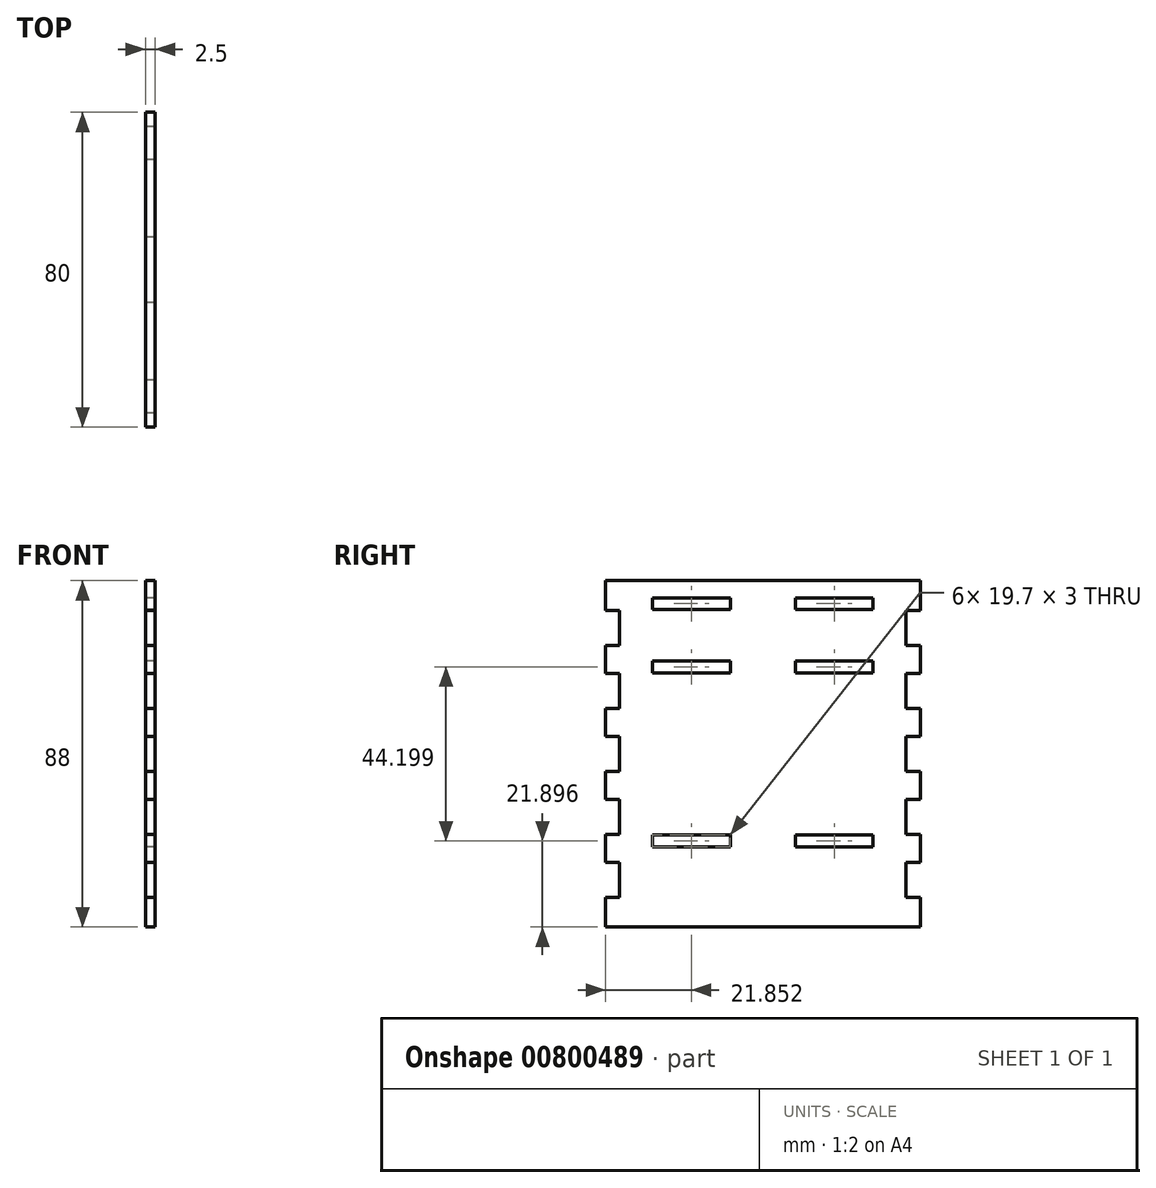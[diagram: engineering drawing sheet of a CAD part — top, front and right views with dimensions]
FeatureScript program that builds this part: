
annotation { "Feature Type Name" : "Feature", "Feature Type Description" : "" }
export const myFeature = defineFeature(function(context is Context, id is Id, definition is map)
    precondition{}
    {
        {
            var Q0;
            Q0=qCreatedBy(makeId("Right.planeOp"),FACE);
            var sketch = newSketch(context, id + "F0", { "sketchPlane" : qUnion([Q0])});
            skLineSegment(sketch, "E0.top", {"start": v(-36.4, -44) * mm, "end": v(36.4, -44) * mm});
            skLineSegment(sketch, "E0.left", {"start": v(-36.4, 44) * mm, "end": v(-36.4, -44) * mm});
            skLineSegment(sketch, "E0.right", {"start": v(36.4, 44) * mm, "end": v(36.4, -44) * mm});
            skPoint(sketch, "E0.middle", {"position": v(0, 0) * mm});
            skLineSegment(sketch, "E1", {"start": v(-36.4, 44) * mm, "end": v(-40, 44) * mm});
            skLineSegment(sketch, "E2", {"start": v(-40, 44) * mm, "end": v(-40, 36.4) * mm});
            skLineSegment(sketch, "E3", {"start": v(-40, 36.4) * mm, "end": v(-36.4, 36.4) * mm});
            skLineSegment(sketch, "E4", {"start": v(-36.4, 36.4) * mm, "end": v(-36.4, 27.6) * mm});
            skLineSegment(sketch, "E5", {"start": v(-36.4, 27.6) * mm, "end": v(-40, 27.6) * mm});
            skLineSegment(sketch, "E6", {"start": v(-40, 27.6) * mm, "end": v(-40, 20.4) * mm});
            skLineSegment(sketch, "E7", {"start": v(-40, 20.4) * mm, "end": v(-36.4, 20.4) * mm});
            skLineSegment(sketch, "E8", {"start": v(-36.4, 20.4) * mm, "end": v(-36.4, 11.6) * mm});
            skLineSegment(sketch, "E9", {"start": v(-36.4, 11.6) * mm, "end": v(-40, 11.6) * mm});
            skLineSegment(sketch, "E10", {"start": v(-40, 11.6) * mm, "end": v(-40, 4.4) * mm});
            skLineSegment(sketch, "E11", {"start": v(-40, 4.4) * mm, "end": v(-36.4, 4.4) * mm});
            skLineSegment(sketch, "E12.MirrorCS", {"start": v(-36.4, -44) * mm, "end": v(-40, -44) * mm});
            skLineSegment(sketch, "E13.MirrorCS", {"start": v(-40, -44) * mm, "end": v(-40, -36.4) * mm});
            skLineSegment(sketch, "E14.MirrorCS", {"start": v(-40, -36.4) * mm, "end": v(-36.4, -36.4) * mm});
            skLineSegment(sketch, "E15.MirrorCS", {"start": v(-36.4, -27.6) * mm, "end": v(-40, -27.6) * mm});
            skLineSegment(sketch, "E16.MirrorCS", {"start": v(-40, -20.4) * mm, "end": v(-36.4, -20.4) * mm});
            skLineSegment(sketch, "E17.MirrorCS", {"start": v(-40, -27.6) * mm, "end": v(-40, -20.4) * mm});
            skLineSegment(sketch, "E18", {"start": v(-36.4, 4.4) * mm, "end": v(-36.4, -4.4) * mm});
            skLineSegment(sketch, "E19", {"start": v(-36.4, -4.4) * mm, "end": v(-40, -4.4) * mm});
            skLineSegment(sketch, "E20", {"start": v(-40, -4.4) * mm, "end": v(-40, -11.6) * mm});
            skLineSegment(sketch, "E21", {"start": v(-40, -11.6) * mm, "end": v(-36.4, -11.6) * mm});
            skLineSegment(sketch, "E22.MirrorCS", {"start": v(36.4, 44) * mm, "end": v(40, 44) * mm});
            skLineSegment(sketch, "E23.MirrorCS", {"start": v(40, 44) * mm, "end": v(40, 36.4) * mm});
            skLineSegment(sketch, "E24.MirrorCS", {"start": v(40, 36.4) * mm, "end": v(36.4, 36.4) * mm});
            skLineSegment(sketch, "E25.MirrorCS", {"start": v(36.4, 27.6) * mm, "end": v(40, 27.6) * mm});
            skLineSegment(sketch, "E26.MirrorCS", {"start": v(40, 27.6) * mm, "end": v(40, 20.4) * mm});
            skLineSegment(sketch, "E27.MirrorCS", {"start": v(40, 20.4) * mm, "end": v(36.4, 20.4) * mm});
            skLineSegment(sketch, "E28.MirrorCS", {"start": v(36.4, 11.6) * mm, "end": v(40, 11.6) * mm});
            skLineSegment(sketch, "E29.MirrorCS", {"start": v(40, 11.6) * mm, "end": v(40, 4.4) * mm});
            skLineSegment(sketch, "E30.MirrorCS", {"start": v(40, 4.4) * mm, "end": v(36.4, 4.4) * mm});
            skLineSegment(sketch, "E31.MirrorCS", {"start": v(36.4, -4.4) * mm, "end": v(40, -4.4) * mm});
            skLineSegment(sketch, "E32.MirrorCS", {"start": v(40, -4.4) * mm, "end": v(40, -11.6) * mm});
            skLineSegment(sketch, "E33.MirrorCS", {"start": v(40, -11.6) * mm, "end": v(36.4, -11.6) * mm});
            skLineSegment(sketch, "E34.MirrorCS", {"start": v(40, -20.4) * mm, "end": v(36.4, -20.4) * mm});
            skLineSegment(sketch, "E35.MirrorCS", {"start": v(40, -27.6) * mm, "end": v(40, -20.4) * mm});
            skLineSegment(sketch, "E36.MirrorCS", {"start": v(36.4, -27.6) * mm, "end": v(40, -27.6) * mm});
            skLineSegment(sketch, "E37.MirrorCS", {"start": v(40, -36.4) * mm, "end": v(36.4, -36.4) * mm});
            skLineSegment(sketch, "E38.MirrorCS", {"start": v(40, -44) * mm, "end": v(40, -36.4) * mm});
            skLineSegment(sketch, "E39.MirrorCS", {"start": v(36.4, -44) * mm, "end": v(40, -44) * mm});
            skPoint(sketch, "E40.middle", {"position": v(-18.15, 38.16) * mm});
            skPoint(sketch, "E41.middle", {"position": v(-18.15, 22.1) * mm});
            skPoint(sketch, "E42.middle", {"position": v(-18.15, -22.1) * mm});
            skLineSegment(sketch, "E43", {"start": v(-36.4, 44) * mm, "end": v(36.4, 44) * mm});
            skLineSegment(sketch, "E44.bottom", {"start": v(-8.3, 36.66) * mm, "end": v(-28, 36.66) * mm});
            skLineSegment(sketch, "E44.top", {"start": v(-8.3, 39.66) * mm, "end": v(-28, 39.66) * mm});
            skLineSegment(sketch, "E44.left", {"start": v(-8.3, 36.66) * mm, "end": v(-8.3, 39.66) * mm});
            skLineSegment(sketch, "E44.right", {"start": v(-28, 36.66) * mm, "end": v(-28, 39.66) * mm});
            skLineSegment(sketch, "E45.bottom", {"start": v(-8.3, 20.6) * mm, "end": v(-28, 20.6) * mm});
            skLineSegment(sketch, "E45.top", {"start": v(-8.3, 23.6) * mm, "end": v(-28, 23.6) * mm});
            skLineSegment(sketch, "E45.left", {"start": v(-8.3, 20.6) * mm, "end": v(-8.3, 23.6) * mm});
            skLineSegment(sketch, "E45.right", {"start": v(-28, 20.6) * mm, "end": v(-28, 23.6) * mm});
            skLineSegment(sketch, "E46.bottom", {"start": v(-28, -20.6) * mm, "end": v(-8.3, -20.6) * mm});
            skLineSegment(sketch, "E46.top", {"start": v(-28, -23.6) * mm, "end": v(-8.3, -23.6) * mm});
            skLineSegment(sketch, "E46.left", {"start": v(-28, -20.6) * mm, "end": v(-28, -23.6) * mm});
            skLineSegment(sketch, "E46.right", {"start": v(-8.3, -20.6) * mm, "end": v(-8.3, -23.6) * mm});
            skLineSegment(sketch, "E47.MirrorCS", {"start": v(8.3, 20.6) * mm, "end": v(8.3, 23.6) * mm});
            skLineSegment(sketch, "E48.MirrorCS", {"start": v(8.3, -20.6) * mm, "end": v(8.3, -23.6) * mm});
            skLineSegment(sketch, "E49.MirrorCS", {"start": v(28, 36.66) * mm, "end": v(28, 39.66) * mm});
            skLineSegment(sketch, "E50.MirrorCS", {"start": v(28, -20.6) * mm, "end": v(28, -23.6) * mm});
            skLineSegment(sketch, "E51.MirrorCS", {"start": v(28, 20.6) * mm, "end": v(28, 23.6) * mm});
            skLineSegment(sketch, "E52.MirrorCS", {"start": v(8.3, 36.66) * mm, "end": v(8.3, 39.66) * mm});
            skPoint(sketch, "E53.MirrorP", {"position": v(18.15, 38.16) * mm});
            skPoint(sketch, "E54.MirrorP", {"position": v(18.15, 22.1) * mm});
            skPoint(sketch, "E55.MirrorP", {"position": v(18.15, -22.1) * mm});
            skLineSegment(sketch, "E56.MirrorCS", {"start": v(8.3, 20.6) * mm, "end": v(28, 20.6) * mm});
            skLineSegment(sketch, "E57.MirrorCS", {"start": v(28, -20.6) * mm, "end": v(8.3, -20.6) * mm});
            skLineSegment(sketch, "E58.MirrorCS", {"start": v(8.3, 39.66) * mm, "end": v(28, 39.66) * mm});
            skLineSegment(sketch, "E59.MirrorCS", {"start": v(28, -23.6) * mm, "end": v(8.3, -23.6) * mm});
            skLineSegment(sketch, "E60.MirrorCS", {"start": v(8.3, 36.66) * mm, "end": v(28, 36.66) * mm});
            skLineSegment(sketch, "E61.MirrorCS", {"start": v(8.3, 23.6) * mm, "end": v(28, 23.6) * mm});
            skSolve(sketch);
        }
        {
            var Q0;
            {var subQ7=sQuery(id+"F0.wireOp",EDGE,"nzJml5v2-Lp1t-HL96-k7b3-nT1KXYDu2QD1.bottom");Q0=makeQuery(id+"F0.imprint","IMPRINT",FACE,{"disambiguationData":[TD([[makeQuery(id+"F0.imprint","IMPRINT",EDGE,{"derivedFrom":subQ7}),-1.0]])]});}
            var Q1;
            {var subQ3=sQuery(id+"F0.wireOp",EDGE,"E9");var subQ9=sQuery(id+"F0.wireOp",EDGE,"E25.MirrorCS");var subQ12=sQuery(id+"F0.wireOp",EDGE,"E5");var subQ17=sQuery(id+"F0.wireOp",EDGE,"E28.MirrorCS");var subQ22=sQuery(id+"F0.wireOp",EDGE,"E15.MirrorCS");var subQ29=sQuery(id+"F0.wireOp",EDGE,"E34.MirrorCS");var subQ32=sQuery(id+"F0.wireOp",EDGE,"E19");var subQ38=sQuery(id+"F0.wireOp",EDGE,"E1");var subQ42=sQuery(id+"F0.wireOp",EDGE,"E12.MirrorCS");var subQ43=sQuery(id+"F0.wireOp",EDGE,"E0.top");var subQ47=sQuery(id+"F0.wireOp",EDGE,"E37.MirrorCS");var subQ51=sQuery(id+"F0.wireOp",EDGE,"E31.MirrorCS");var subQ57=sQuery(id+"F0.wireOp",EDGE,"E22.MirrorCS");Q1=qUnion([makeQuery(id+"F0.imprint","IMPRINT",FACE,{"disambiguationData":[TD([[makeQuery(id+"F0.imprint","IMPRINT",EDGE,{"derivedFrom":subQ47}),1.0]])]}),makeQuery(id+"F0.imprint","IMPRINT",FACE,{"disambiguationData":[TD([[makeQuery(id+"F0.imprint","IMPRINT",EDGE,{"derivedFrom":subQ42}),-1.0]])]}),makeQuery(id+"F0.imprint","IMPRINT",FACE,{"disambiguationData":[TD([[makeQuery(id+"F0.imprint","IMPRINT",EDGE,{"derivedFrom":subQ57}),-1.0]])]}),makeQuery(id+"F0.imprint","IMPRINT",FACE,{"disambiguationData":[TD([[makeQuery(id+"F0.imprint","IMPRINT",EDGE,{"derivedFrom":subQ38}),1.0]])]}),makeQuery(id+"F0.imprint","IMPRINT",FACE,{"disambiguationData":[TD([[makeQuery(id+"F0.imprint","IMPRINT",EDGE,{"derivedFrom":subQ51}),-1.0]])]}),makeQuery(id+"F0.imprint","IMPRINT",FACE,{"disambiguationData":[TD([[makeQuery(id+"F0.imprint","IMPRINT",EDGE,{"derivedFrom":subQ32}),1.0]])]}),makeQuery(id+"F0.imprint","IMPRINT",FACE,{"disambiguationData":[TD([[makeQuery(id+"F0.imprint","IMPRINT",EDGE,{"derivedFrom":subQ43}),1.0]])]}),makeQuery(id+"F0.imprint","IMPRINT",FACE,{"disambiguationData":[TD([[makeQuery(id+"F0.imprint","IMPRINT",EDGE,{"derivedFrom":subQ29}),1.0]])]}),makeQuery(id+"F0.imprint","IMPRINT",FACE,{"disambiguationData":[TD([[makeQuery(id+"F0.imprint","IMPRINT",EDGE,{"derivedFrom":subQ22}),-1.0]])]}),makeQuery(id+"F0.imprint","IMPRINT",FACE,{"disambiguationData":[TD([[makeQuery(id+"F0.imprint","IMPRINT",EDGE,{"derivedFrom":subQ17}),-1.0]])]}),makeQuery(id+"F0.imprint","IMPRINT",FACE,{"disambiguationData":[TD([[makeQuery(id+"F0.imprint","IMPRINT",EDGE,{"derivedFrom":subQ12}),1.0]])]}),makeQuery(id+"F0.imprint","IMPRINT",FACE,{"disambiguationData":[TD([[makeQuery(id+"F0.imprint","IMPRINT",EDGE,{"derivedFrom":subQ9}),-1.0]])]}),makeQuery(id+"F0.imprint","IMPRINT",FACE,{"disambiguationData":[TD([[makeQuery(id+"F0.imprint","IMPRINT",EDGE,{"derivedFrom":subQ3}),1.0]])]})]);}
            extrude(context, id + "F1", {"entities" : qUnion([Q0, Q1]), "depth" : 2.5 * mm, "offsetDistance" : 25 * mm});
        }
    });
